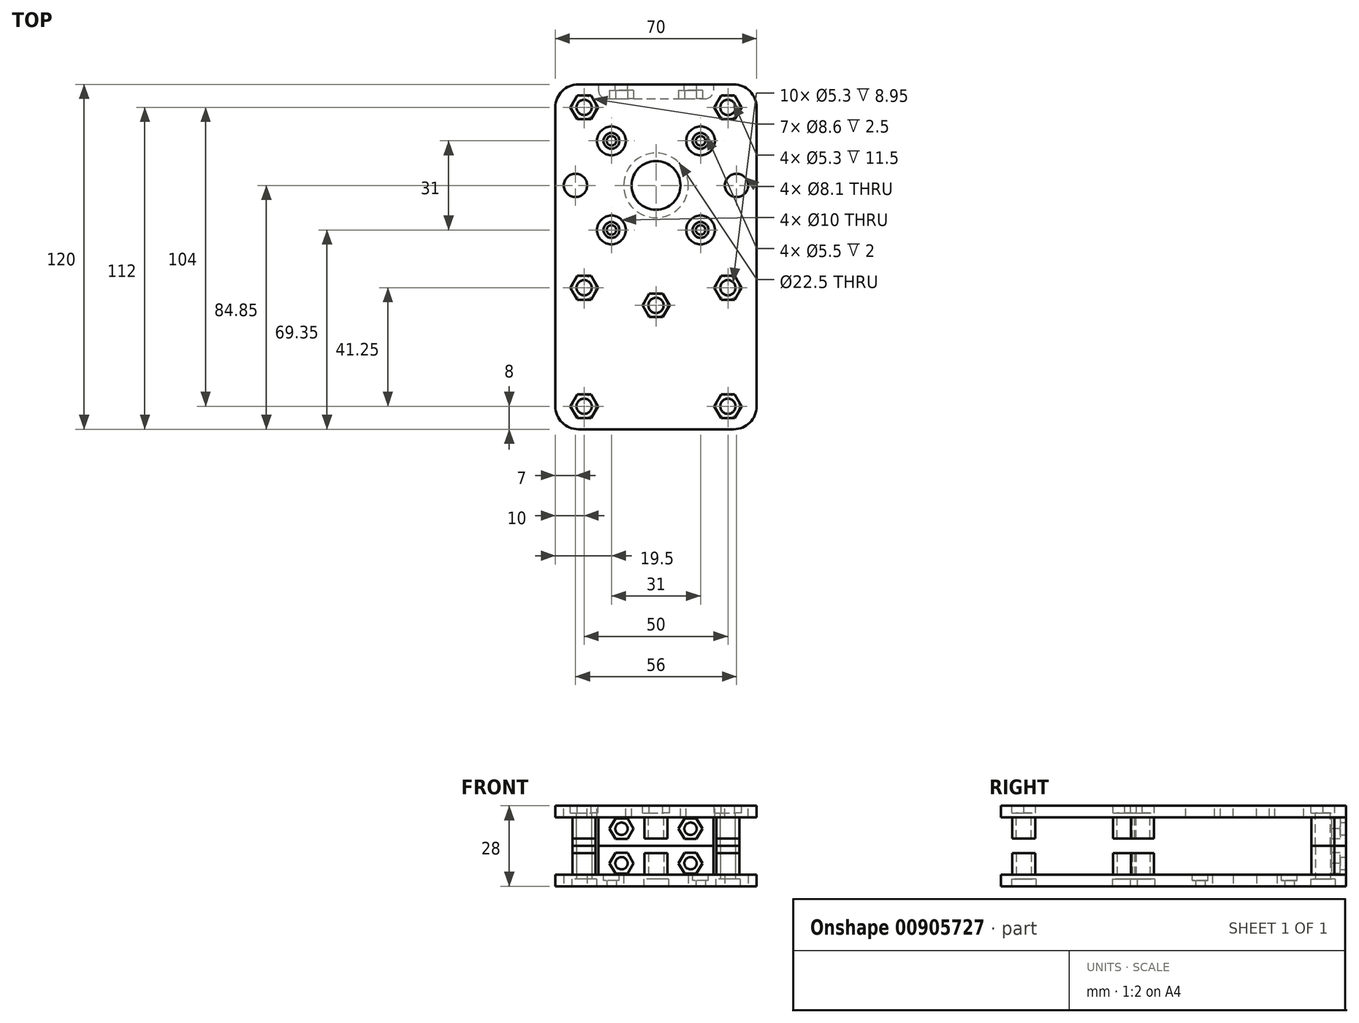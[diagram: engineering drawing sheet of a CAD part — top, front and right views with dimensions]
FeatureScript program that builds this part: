
annotation { "Feature Type Name" : "Feature", "Feature Type Description" : "" }
export const myFeature = defineFeature(function(context is Context, id is Id, definition is map)
    precondition{}
    {
        {
            var Q0;
            Q0=qCreatedBy(makeId("Top.planeOp"),FACE);
            var sketch = newSketch(context, id + "F0", { "sketchPlane" : qUnion([Q0])});
            skLineSegment(sketch, "E0.bottom", {"start": v(-35, 60) * mm, "end": v(35, 60) * mm});
            skLineSegment(sketch, "E0.top", {"start": v(-35, -60) * mm, "end": v(35, -60) * mm});
            skLineSegment(sketch, "E0.left", {"start": v(-35, 60) * mm, "end": v(-35, -60) * mm});
            skLineSegment(sketch, "E0.right", {"start": v(35, 60) * mm, "end": v(35, -60) * mm});
            skPoint(sketch, "E0.middle", {"position": v(0, 0) * mm});
            skCircle(sketch, "E1", {"center": v(-25, -52) * mm, "radius": 2.65 * mm});
            skCircle(sketch, "E2", {"center": v(25, -52) * mm, "radius": 2.65 * mm});
            skCircle(sketch, "E3", {"center": v(-25, 52) * mm, "radius": 2.65 * mm});
            skCircle(sketch, "E4", {"center": v(25, 52) * mm, "radius": 2.65 * mm});
            skCircle(sketch, "E5", {"center": v(-25, -52) * mm, "radius": 10.75 * mm, "construction": true});
            skCircle(sketch, "E6", {"center": v(25, -52) * mm, "radius": 10.75 * mm, "construction": true});
            skLineSegment(sketch, "E7.bottom", {"start": v(-50, -26.75) * mm, "end": v(50, -26.75) * mm, "construction": true});
            skLineSegment(sketch, "E7.top", {"start": v(-50, -41.75) * mm, "end": v(50, -41.75) * mm, "construction": true});
            skLineSegment(sketch, "E7.left", {"start": v(-50, -26.75) * mm, "end": v(-50, -41.75) * mm, "construction": true});
            skLineSegment(sketch, "E7.right", {"start": v(50, -26.75) * mm, "end": v(50, -41.75) * mm, "construction": true});
            skPoint(sketch, "E7.middle", {"position": v(0, -34.25) * mm});
            skLineSegment(sketch, "E8.bottom", {"start": v(-1.65, -11.6) * mm, "end": v(1.65, -11.6) * mm, "construction": true});
            skLineSegment(sketch, "E8.top", {"start": v(-1.65, -22.2) * mm, "end": v(1.65, -22.2) * mm, "construction": true});
            skLineSegment(sketch, "E8.left", {"start": v(-2.65, -12.6) * mm, "end": v(-2.65, -21.2) * mm, "construction": true});
            skLineSegment(sketch, "E8.right", {"start": v(2.65, -12.6) * mm, "end": v(2.65, -21.2) * mm, "construction": true});
            skPoint(sketch, "E8.middle", {"position": v(0, -16.9) * mm});
            skPoint(sketch, "E9.visualSharp", {"position": v(-2.65, -22.2) * mm});
            skArc(sketch, "E9.filletArc", {"start": v(-2.65, -21.2) * mm, "mid": v(-2.36, -21.9) * mm, "end": v(-1.65, -22.2) * mm, "construction": true});
            skPoint(sketch, "E10.visualSharp", {"position": v(2.65, -22.2) * mm});
            skArc(sketch, "E10.filletArc", {"start": v(1.65, -22.2) * mm, "mid": v(2.36, -21.9) * mm, "end": v(2.65, -21.2) * mm, "construction": true});
            skPoint(sketch, "E11.visualSharp", {"position": v(2.65, -11.6) * mm});
            skArc(sketch, "E11.filletArc", {"start": v(2.65, -12.6) * mm, "mid": v(2.36, -11.9) * mm, "end": v(1.65, -11.6) * mm, "construction": true});
            skPoint(sketch, "E12.visualSharp", {"position": v(-2.65, -11.6) * mm});
            skArc(sketch, "E12.filletArc", {"start": v(-1.65, -11.6) * mm, "mid": v(-2.36, -11.9) * mm, "end": v(-2.65, -12.6) * mm, "construction": true});
            skCircle(sketch, "E13", {"center": v(0, -16.9) * mm, "radius": 10.75 * mm, "construction": true});
            skCircle(sketch, "E14", {"center": v(-25, -10.75) * mm, "radius": 2.65 * mm});
            skCircle(sketch, "E15", {"center": v(25, -10.75) * mm, "radius": 2.65 * mm});
            skCircle(sketch, "E16", {"center": v(-25, -10.75) * mm, "radius": 11 * mm, "construction": true});
            skCircle(sketch, "E17", {"center": v(25, -10.75) * mm, "radius": 11 * mm, "construction": true});
            skLineSegment(sketch, "E18.bottom", {"start": v(-21.15, 46) * mm, "end": v(21.15, 46) * mm, "construction": true});
            skLineSegment(sketch, "E18.top", {"start": v(-21.15, 3.7) * mm, "end": v(21.15, 3.7) * mm, "construction": true});
            skLineSegment(sketch, "E18.left", {"start": v(-21.15, 46) * mm, "end": v(-21.15, 3.7) * mm, "construction": true});
            skLineSegment(sketch, "E18.right", {"start": v(21.15, 46) * mm, "end": v(21.15, 3.7) * mm, "construction": true});
            skPoint(sketch, "E18.middle", {"position": v(0, 24.85) * mm});
            skCircle(sketch, "E19", {"center": v(-25, 52) * mm, "radius": 4.3 * mm});
            skCircle(sketch, "E20", {"center": v(25, 52) * mm, "radius": 4.3 * mm});
            skCircle(sketch, "E21", {"center": v(-25, -10.75) * mm, "radius": 4.3 * mm});
            skCircle(sketch, "E22", {"center": v(25, -10.75) * mm, "radius": 4.3 * mm});
            skCircle(sketch, "E23", {"center": v(-25, -52) * mm, "radius": 4.3 * mm});
            skCircle(sketch, "E24", {"center": v(25, -52) * mm, "radius": 4.3 * mm});
            skCircle(sketch, "E25", {"center": v(-28, 24.85) * mm, "radius": 4.05 * mm});
            skCircle(sketch, "E26", {"center": v(28, 24.85) * mm, "radius": 4.05 * mm});
            skCircle(sketch, "E27", {"center": v(-15.5, 40.35) * mm, "radius": 1.65 * mm});
            skCircle(sketch, "E28", {"center": v(15.5, 40.35) * mm, "radius": 1.65 * mm});
            skCircle(sketch, "E29", {"center": v(15.5, 9.35) * mm, "radius": 1.65 * mm});
            skCircle(sketch, "E30", {"center": v(-15.5, 9.35) * mm, "radius": 1.65 * mm});
            skCircle(sketch, "E31", {"center": v(0, 24.85) * mm, "radius": 11.25 * mm});
            skCircle(sketch, "E32", {"center": v(0, -16.9) * mm, "radius": 2.65 * mm});
            skCircle(sketch, "E33", {"center": v(0, -16.9) * mm, "radius": 4.3 * mm});
            skSolve(sketch);
        }
        {
            var Q0;
            Q0=makeQuery(id+"F0.imprint","IMPRINT",FACE,{"disambiguationData":[TD([[makeQuery(id+"F0.imprint","IMPRINT",EDGE,{"derivedFrom":sQuery(id+"F0.wireOp",EDGE,"E0.bottom")}),-1.0]])]});
            var Q1;
            Q1=makeQuery(id+"F0.imprint","IMPRINT",FACE,{"disambiguationData":[TD([[makeQuery(id+"F0.imprint","IMPRINT",EDGE,{"derivedFrom":sQuery(id+"F0.wireOp",EDGE,"E4")}),-1.0]])]});
            var Q2;
            Q2=makeQuery(id+"F0.imprint","IMPRINT",FACE,{"disambiguationData":[TD([[makeQuery(id+"F0.imprint","IMPRINT",EDGE,{"derivedFrom":sQuery(id+"F0.wireOp",EDGE,"E3")}),-1.0]])]});
            var Q3;
            Q3=makeQuery(id+"F0.imprint","IMPRINT",FACE,{"disambiguationData":[TD([[makeQuery(id+"F0.imprint","IMPRINT",EDGE,{"derivedFrom":sQuery(id+"F0.wireOp",EDGE,"E15")}),-1.0]])]});
            var Q4;
            Q4=makeQuery(id+"F0.imprint","IMPRINT",FACE,{"disambiguationData":[TD([[makeQuery(id+"F0.imprint","IMPRINT",EDGE,{"derivedFrom":sQuery(id+"F0.wireOp",EDGE,"E14")}),-1.0]])]});
            var Q5;
            Q5=makeQuery(id+"F0.imprint","IMPRINT",FACE,{"disambiguationData":[TD([[makeQuery(id+"F0.imprint","IMPRINT",EDGE,{"derivedFrom":sQuery(id+"F0.wireOp",EDGE,"E2")}),-1.0]])]});
            var Q6;
            Q6=makeQuery(id+"F0.imprint","IMPRINT",FACE,{"disambiguationData":[TD([[makeQuery(id+"F0.imprint","IMPRINT",EDGE,{"derivedFrom":sQuery(id+"F0.wireOp",EDGE,"E1")}),-1.0]])]});
            var Q7;
            Q7=makeQuery(id+"F0.imprint","IMPRINT",FACE,{"disambiguationData":[TD([[makeQuery(id+"F0.imprint","IMPRINT",EDGE,{"derivedFrom":sQuery(id+"F0.wireOp",EDGE,"E32")}),-1.0]])]});
            extrude(context, id + "F1", {"entities" : qUnion([Q0, Q1, Q2, Q3, Q4, Q5, Q6, Q7]), "depth" : 4 * mm, "offsetDistance" : 25 * mm});
        }
        {
            var Q0;
            Q0=makeQuery(id+"F1.opExtrude","CAP_FACE",FACE,{"disambiguationData":[OSD([sQuery(id+"F0.wireOp",EDGE,"E0.bottom"),sQuery(id+"F0.wireOp",EDGE,"E0.top"),sQuery(id+"F0.wireOp",EDGE,"E0.left"),sQuery(id+"F0.wireOp",EDGE,"E0.right"),sQuery(id+"F0.wireOp",EDGE,"E1"),sQuery(id+"F0.wireOp",EDGE,"E2"),sQuery(id+"F0.wireOp",EDGE,"E3"),sQuery(id+"F0.wireOp",EDGE,"E4"),sQuery(id+"F0.wireOp",EDGE,"E8.bottom"),sQuery(id+"F0.wireOp",EDGE,"E8.top"),sQuery(id+"F0.wireOp",EDGE,"E8.left"),sQuery(id+"F0.wireOp",EDGE,"E8.right"),sQuery(id+"F0.wireOp",EDGE,"E9.filletArc"),sQuery(id+"F0.wireOp",EDGE,"E10.filletArc"),sQuery(id+"F0.wireOp",EDGE,"E11.filletArc"),sQuery(id+"F0.wireOp",EDGE,"E12.filletArc"),sQuery(id+"F0.wireOp",EDGE,"E14"),sQuery(id+"F0.wireOp",EDGE,"E15"),sQuery(id+"F0.wireOp",EDGE,"E25"),sQuery(id+"F0.wireOp",EDGE,"E26"),sQuery(id+"F0.wireOp",EDGE,"E27"),sQuery(id+"F0.wireOp",EDGE,"E28"),sQuery(id+"F0.wireOp",EDGE,"E29"),sQuery(id+"F0.wireOp",EDGE,"E30"),sQuery(id+"F0.wireOp",EDGE,"E31")])],"isStart":false});
            var sketch = newSketch(context, id + "F2", { "sketchPlane" : qUnion([Q0])});
            skCircle(sketch, "E34", {"center": v(-15.5, 40.35) * mm, "radius": 2.75 * mm});
            skCircle(sketch, "E35", {"center": v(15.5, 40.35) * mm, "radius": 2.75 * mm});
            skCircle(sketch, "E36", {"center": v(-15.5, 9.35) * mm, "radius": 2.75 * mm});
            skCircle(sketch, "E37", {"center": v(15.5, 9.35) * mm, "radius": 2.75 * mm});
            skSolve(sketch);
        }
        {
            var Q0;
            Q0=makeQuery(id+"F2.imprint","IMPRINT",FACE,{"disambiguationData":[TD([[makeQuery(id+"F2.imprint","IMPRINT",EDGE,{"derivedFrom":sQuery(id+"F2.wireOp",EDGE,"E34")}),1.0]])]});
            var Q1;
            Q1=makeQuery(id+"F2.imprint","IMPRINT",FACE,{"disambiguationData":[TD([[makeQuery(id+"F2.imprint","IMPRINT",EDGE,{"derivedFrom":sQuery(id+"F2.wireOp",EDGE,"E36")}),1.0]])]});
            var Q2;
            Q2=makeQuery(id+"F2.imprint","IMPRINT",FACE,{"disambiguationData":[TD([[makeQuery(id+"F2.imprint","IMPRINT",EDGE,{"derivedFrom":sQuery(id+"F2.wireOp",EDGE,"E37")}),1.0]])]});
            var Q3;
            Q3=makeQuery(id+"F2.imprint","IMPRINT",FACE,{"disambiguationData":[TD([[makeQuery(id+"F2.imprint","IMPRINT",EDGE,{"derivedFrom":sQuery(id+"F2.wireOp",EDGE,"E35")}),1.0]])]});
            extrude(context, id + "F3", {"entities" : qUnion([Q0, Q1, Q2, Q3]), "operationType" : NewBodyOperationType.REMOVE, "oppositeDirection" : true, "depth" : 2 * mm, "offsetDistance" : 25 * mm});
        }
        {
            var Q0;
            Q0=makeQuery(id+"F0.imprint","IMPRINT",FACE,{"disambiguationData":[TD([[makeQuery(id+"F0.imprint","IMPRINT",EDGE,{"derivedFrom":sQuery(id+"F0.wireOp",EDGE,"E4")}),-1.0]])]});
            var Q1;
            Q1=makeQuery(id+"F0.imprint","IMPRINT",FACE,{"disambiguationData":[TD([[makeQuery(id+"F0.imprint","IMPRINT",EDGE,{"derivedFrom":sQuery(id+"F0.wireOp",EDGE,"E3")}),-1.0]])]});
            var Q2;
            Q2=makeQuery(id+"F0.imprint","IMPRINT",FACE,{"disambiguationData":[TD([[makeQuery(id+"F0.imprint","IMPRINT",EDGE,{"derivedFrom":sQuery(id+"F0.wireOp",EDGE,"E15")}),-1.0]])]});
            var Q3;
            Q3=makeQuery(id+"F0.imprint","IMPRINT",FACE,{"disambiguationData":[TD([[makeQuery(id+"F0.imprint","IMPRINT",EDGE,{"derivedFrom":sQuery(id+"F0.wireOp",EDGE,"E14")}),-1.0]])]});
            var Q4;
            Q4=makeQuery(id+"F0.imprint","IMPRINT",FACE,{"disambiguationData":[TD([[makeQuery(id+"F0.imprint","IMPRINT",EDGE,{"derivedFrom":sQuery(id+"F0.wireOp",EDGE,"E2")}),-1.0]])]});
            var Q5;
            Q5=makeQuery(id+"F0.imprint","IMPRINT",FACE,{"disambiguationData":[TD([[makeQuery(id+"F0.imprint","IMPRINT",EDGE,{"derivedFrom":sQuery(id+"F0.wireOp",EDGE,"E1")}),-1.0]])]});
            extrude(context, id + "F4", {"entities" : qUnion([Q0, Q1, Q2, Q3, Q4, Q5]), "operationType" : NewBodyOperationType.REMOVE, "depth" : 2.5 * mm, "offsetDistance" : 25 * mm});
        }
        {
            var Q0;
            Q0=makeQuery(id+"FN2gQwAAYemFBsZ_1.imprint","IMPRINT",FACE,{"disambiguationData":[TD([[makeQuery(id+"FN2gQwAAYemFBsZ_1.imprint","IMPRINT",EDGE,{"derivedFrom":sQuery(id+"FN2gQwAAYemFBsZ_1.wireOp",EDGE,"b6049740-b090-4d88-954d-f700c698196f.0")}),1.0]])]});
            var Q1;
            Q1=makeQuery(id+"F0.imprint","IMPRINT",FACE,{"disambiguationData":[TD([[makeQuery(id+"F0.imprint","IMPRINT",EDGE,{"derivedFrom":sQuery(id+"F0.wireOp",EDGE,"E32")}),-1.0]])]});
            extrude(context, id + "F5", {"entities" : qUnion([Q0, Q1]), "operationType" : NewBodyOperationType.REMOVE, "depth" : 2.5 * mm, "offsetDistance" : 25 * mm});
        }
        {
            var Q0;
            Q0=makeQuery(id+"F1.opExtrude","CAP_FACE",FACE,{"disambiguationData":[OSD([sQuery(id+"F0.wireOp",EDGE,"E0.bottom"),sQuery(id+"F0.wireOp",EDGE,"E0.top"),sQuery(id+"F0.wireOp",EDGE,"E0.left"),sQuery(id+"F0.wireOp",EDGE,"E0.right"),sQuery(id+"F0.wireOp",EDGE,"E1"),sQuery(id+"F0.wireOp",EDGE,"E2"),sQuery(id+"F0.wireOp",EDGE,"E3"),sQuery(id+"F0.wireOp",EDGE,"E4"),sQuery(id+"F0.wireOp",EDGE,"E8.bottom"),sQuery(id+"F0.wireOp",EDGE,"E8.top"),sQuery(id+"F0.wireOp",EDGE,"E8.left"),sQuery(id+"F0.wireOp",EDGE,"E8.right"),sQuery(id+"F0.wireOp",EDGE,"E9.filletArc"),sQuery(id+"F0.wireOp",EDGE,"E10.filletArc"),sQuery(id+"F0.wireOp",EDGE,"E11.filletArc"),sQuery(id+"F0.wireOp",EDGE,"E12.filletArc"),sQuery(id+"F0.wireOp",EDGE,"E14"),sQuery(id+"F0.wireOp",EDGE,"E15"),sQuery(id+"F0.wireOp",EDGE,"E25"),sQuery(id+"F0.wireOp",EDGE,"E26"),sQuery(id+"F0.wireOp",EDGE,"E27"),sQuery(id+"F0.wireOp",EDGE,"E28"),sQuery(id+"F0.wireOp",EDGE,"E29"),sQuery(id+"F0.wireOp",EDGE,"E30"),sQuery(id+"F0.wireOp",EDGE,"E31")])],"isStart":false});
            var sketch = newSketch(context, id + "F6", { "sketchPlane" : qUnion([Q0])});
            skCircle(sketch, "E38", {"center": v(-25, -10.75) * mm, "radius": 4 * mm});
            skCircle(sketch, "E39", {"center": v(-25, -52) * mm, "radius": 4 * mm});
            skCircle(sketch, "E40", {"center": v(25, -52) * mm, "radius": 4 * mm});
            skCircle(sketch, "E41", {"center": v(25, -10.75) * mm, "radius": 4 * mm});
            skCircle(sketch, "E42", {"center": v(-25, 52) * mm, "radius": 4 * mm});
            skCircle(sketch, "E43", {"center": v(25, 52) * mm, "radius": 4 * mm});
            skCircle(sketch, "E44", {"center": v(0, -16.9) * mm, "radius": 4 * mm});
            skSolve(sketch);
        }
        {
            var Q0;
            Q0=makeQuery(id+"F6.imprint","IMPRINT",FACE,{"disambiguationData":[TD([[makeQuery(id+"F6.imprint","IMPRINT",EDGE,{"derivedFrom":sQuery(id+"F6.wireOp",EDGE,"E38")}),1.0]])]});
            var Q1;
            Q1=makeQuery(id+"F6.imprint","IMPRINT",FACE,{"disambiguationData":[TD([[makeQuery(id+"F6.imprint","IMPRINT",EDGE,{"derivedFrom":sQuery(id+"F6.wireOp",EDGE,"E39")}),1.0]])]});
            var Q2;
            Q2=makeQuery(id+"F6.imprint","IMPRINT",FACE,{"disambiguationData":[TD([[makeQuery(id+"F6.imprint","IMPRINT",EDGE,{"derivedFrom":sQuery(id+"F6.wireOp",EDGE,"E40")}),1.0]])]});
            var Q3;
            Q3=makeQuery(id+"F6.imprint","IMPRINT",FACE,{"disambiguationData":[TD([[makeQuery(id+"F6.imprint","IMPRINT",EDGE,{"derivedFrom":sQuery(id+"F6.wireOp",EDGE,"E41")}),1.0]])]});
            var Q4;
            Q4=makeQuery(id+"F6.imprint","IMPRINT",FACE,{"disambiguationData":[TD([[makeQuery(id+"F6.imprint","IMPRINT",EDGE,{"derivedFrom":sQuery(id+"F6.wireOp",EDGE,"E44")}),1.0]])]});
            extrude(context, id + "F7", {"entities" : qUnion([Q0, Q1, Q2, Q3, Q4]), "operationType" : NewBodyOperationType.ADD, "depth" : 7.45 * mm, "offsetDistance" : 25 * mm});
        }
        {
            var Q0;
            Q0=makeQuery(id+"F6.imprint","IMPRINT",FACE,{"disambiguationData":[TD([[makeQuery(id+"F6.imprint","IMPRINT",EDGE,{"derivedFrom":sQuery(id+"F6.wireOp",EDGE,"E42")}),1.0]])]});
            var Q1;
            Q1=makeQuery(id+"F6.imprint","IMPRINT",FACE,{"disambiguationData":[TD([[makeQuery(id+"F6.imprint","IMPRINT",EDGE,{"derivedFrom":sQuery(id+"F6.wireOp",EDGE,"E43")}),1.0]])]});
            extrude(context, id + "F8", {"entities" : qUnion([Q0, Q1]), "operationType" : NewBodyOperationType.ADD, "depth" : 10 * mm, "offsetDistance" : 25 * mm});
        }
        {
            var Q0;
            Q0=makeQuery(id+"F1.opExtrude","CAP_FACE",FACE,{"disambiguationData":[OSD([sQuery(id+"F0.wireOp",EDGE,"E0.bottom"),sQuery(id+"F0.wireOp",EDGE,"E0.top"),sQuery(id+"F0.wireOp",EDGE,"E0.left"),sQuery(id+"F0.wireOp",EDGE,"E0.right"),sQuery(id+"F0.wireOp",EDGE,"E1"),sQuery(id+"F0.wireOp",EDGE,"E2"),sQuery(id+"F0.wireOp",EDGE,"E3"),sQuery(id+"F0.wireOp",EDGE,"E4"),sQuery(id+"F0.wireOp",EDGE,"E8.bottom"),sQuery(id+"F0.wireOp",EDGE,"E8.top"),sQuery(id+"F0.wireOp",EDGE,"E8.left"),sQuery(id+"F0.wireOp",EDGE,"E8.right"),sQuery(id+"F0.wireOp",EDGE,"E9.filletArc"),sQuery(id+"F0.wireOp",EDGE,"E10.filletArc"),sQuery(id+"F0.wireOp",EDGE,"E11.filletArc"),sQuery(id+"F0.wireOp",EDGE,"E12.filletArc"),sQuery(id+"F0.wireOp",EDGE,"E14"),sQuery(id+"F0.wireOp",EDGE,"E15"),sQuery(id+"F0.wireOp",EDGE,"E25"),sQuery(id+"F0.wireOp",EDGE,"E26"),sQuery(id+"F0.wireOp",EDGE,"E27"),sQuery(id+"F0.wireOp",EDGE,"E28"),sQuery(id+"F0.wireOp",EDGE,"E29"),sQuery(id+"F0.wireOp",EDGE,"E30"),sQuery(id+"F0.wireOp",EDGE,"E31")])],"isStart":false});
            var sketch = newSketch(context, id + "F9", { "sketchPlane" : qUnion([Q0])});
            skLineSegment(sketch, "E45.bottom", {"start": v(-20, 60) * mm, "end": v(20, 60) * mm});
            skLineSegment(sketch, "E45.top", {"start": v(-17, 55) * mm, "end": v(17, 55) * mm});
            skLineSegment(sketch, "E45.left", {"start": v(-20, 60) * mm, "end": v(-20, 58) * mm});
            skLineSegment(sketch, "E45.right", {"start": v(20, 60) * mm, "end": v(20, 58) * mm});
            skPoint(sketch, "E46.visualSharp", {"position": v(-20, 55) * mm});
            skArc(sketch, "E46.filletArc", {"start": v(-20, 58) * mm, "mid": v(-19.12, 55.88) * mm, "end": v(-17, 55) * mm});
            skPoint(sketch, "E47.visualSharp", {"position": v(20, 55) * mm});
            skArc(sketch, "E47.filletArc", {"start": v(17, 55) * mm, "mid": v(19.12, 55.88) * mm, "end": v(20, 58) * mm});
            skSolve(sketch);
        }
        {
            var Q0;
            Q0=makeQuery(id+"F9.imprint","IMPRINT",FACE,{"disambiguationData":[TD([[makeQuery(id+"F9.imprint","IMPRINT",EDGE,{"derivedFrom":sQuery(id+"F9.wireOp",EDGE,"E45.bottom")}),-1.0]])]});
            extrude(context, id + "F10", {"entities" : qUnion([Q0]), "operationType" : NewBodyOperationType.ADD, "depth" : 10 * mm, "offsetDistance" : 25 * mm});
        }
        {
            var Q0;
            Q0=makeQuery(id+"F10.boolean.opBoolean","MERGE",FACE,{"derivedFrom":[makeQuery(id+"F1.opExtrude","SWEPT_FACE",FACE,{"disambiguationData":[OSD([sQuery(id+"F0.wireOp",EDGE,"E0.bottom")])]}),makeQuery(id+"F10.opExtrude","SWEPT_FACE",FACE,{"disambiguationData":[OSD([sQuery(id+"F9.wireOp",EDGE,"E45.bottom")])]})]});
            var sketch = newSketch(context, id + "F11", { "sketchPlane" : qUnion([Q0])});
            skCircle(sketch, "E48", {"center": v(12, 8) * mm, "radius": 2.15 * mm});
            skCircle(sketch, "E49", {"center": v(-12, 8) * mm, "radius": 2.15 * mm});
            skSolve(sketch);
        }
        {
            var Q0;
            Q0=makeQuery(id+"F11.imprint","IMPRINT",FACE,{"disambiguationData":[TD([[makeQuery(id+"F11.imprint","IMPRINT",EDGE,{"derivedFrom":sQuery(id+"F11.wireOp",EDGE,"E48")}),1.0]])]});
            var Q1;
            Q1=makeQuery(id+"F11.imprint","IMPRINT",FACE,{"disambiguationData":[TD([[makeQuery(id+"F11.imprint","IMPRINT",EDGE,{"derivedFrom":sQuery(id+"F11.wireOp",EDGE,"E49")}),1.0]])]});
            var Q2;
            Q2=makeQuery(id+"F10.opExtrude","SWEPT_FACE",FACE,{"disambiguationData":[OSD([sQuery(id+"F9.wireOp",EDGE,"E45.top")])]});
            extrude(context, id + "F12", {"entities" : qUnion([Q0, Q1]), "operationType" : NewBodyOperationType.REMOVE, "endBound" : BoundingType.UP_TO_SURFACE, "oppositeDirection" : true, "depth" : 25 * mm, "endBoundEntityFace" : qUnion([Q2]), "offsetDistance" : 25 * mm});
        }
        {
            var Q0;
            Q0=makeQuery(id+"F10.opExtrude","SWEPT_FACE",FACE,{"disambiguationData":[OSD([sQuery(id+"F9.wireOp",EDGE,"E45.top")])]});
            var sketch = newSketch(context, id + "F13", { "sketchPlane" : qUnion([Q0])});
            skCircle(sketch, "E50.cCircle", {"center": v(-12, 8) * mm, "radius": 3.6 * mm, "construction": true});
            skLineSegment(sketch, "E50.0", {"start": v(-14.08, 11.6) * mm, "end": v(-9.92, 11.6) * mm});
            skLineSegment(sketch, "E50.1", {"start": v(-9.92, 11.6) * mm, "end": v(-7.84, 8) * mm});
            skLineSegment(sketch, "E50.2", {"start": v(-7.84, 8) * mm, "end": v(-9.92, 4.4) * mm});
            skLineSegment(sketch, "E50.3", {"start": v(-9.92, 4.4) * mm, "end": v(-14.08, 4.4) * mm});
            skLineSegment(sketch, "E50.4", {"start": v(-14.08, 4.4) * mm, "end": v(-16.16, 8) * mm});
            skLineSegment(sketch, "E50.5", {"start": v(-16.16, 8) * mm, "end": v(-14.08, 11.6) * mm});
            skPoint(sketch, "E50.0.midPoint", {"position": v(-12, 11.6) * mm});
            skCircle(sketch, "E51.cCircle", {"center": v(12, 8) * mm, "radius": 3.6 * mm, "construction": true});
            skLineSegment(sketch, "E51.0", {"start": v(9.92, 11.6) * mm, "end": v(14.08, 11.6) * mm});
            skLineSegment(sketch, "E51.1", {"start": v(14.08, 11.6) * mm, "end": v(16.16, 8) * mm});
            skLineSegment(sketch, "E51.2", {"start": v(16.16, 8) * mm, "end": v(14.08, 4.4) * mm});
            skLineSegment(sketch, "E51.3", {"start": v(14.08, 4.4) * mm, "end": v(9.92, 4.4) * mm});
            skLineSegment(sketch, "E51.4", {"start": v(9.92, 4.4) * mm, "end": v(7.84, 8) * mm});
            skLineSegment(sketch, "E51.5", {"start": v(7.84, 8) * mm, "end": v(9.92, 11.6) * mm});
            skPoint(sketch, "E51.0.midPoint", {"position": v(12, 11.6) * mm});
            skSolve(sketch);
        }
        {
            var Q0;
            Q0=makeQuery(id+"F13.imprint","IMPRINT",FACE,{"disambiguationData":[TD([[makeQuery(id+"F13.imprint","IMPRINT",EDGE,{"derivedFrom":sQuery(id+"F13.wireOp",EDGE,"E51.0")}),-1.0]])]});
            var Q1;
            Q1=makeQuery(id+"F13.imprint","IMPRINT",FACE,{"disambiguationData":[TD([[makeQuery(id+"F13.imprint","IMPRINT",EDGE,{"derivedFrom":sQuery(id+"F13.wireOp",EDGE,"E50.0")}),-1.0]])]});
            extrude(context, id + "F14", {"entities" : qUnion([Q0, Q1]), "operationType" : NewBodyOperationType.REMOVE, "oppositeDirection" : true, "depth" : 3 * mm, "offsetDistance" : 25 * mm});
        }
        {
            var Q0;
            Q0=makeQuery(id+"F1.opExtrude","SWEPT_BODY",BODY,{"disambiguationData":[OSD([sQuery(id+"F0.wireOp",EDGE,"E0.bottom"),sQuery(id+"F0.wireOp",EDGE,"E0.top"),sQuery(id+"F0.wireOp",EDGE,"E0.left"),sQuery(id+"F0.wireOp",EDGE,"E0.right"),sQuery(id+"F0.wireOp",EDGE,"E1"),sQuery(id+"F0.wireOp",EDGE,"E2"),sQuery(id+"F0.wireOp",EDGE,"E3"),sQuery(id+"F0.wireOp",EDGE,"E4"),sQuery(id+"F0.wireOp",EDGE,"E8.bottom"),sQuery(id+"F0.wireOp",EDGE,"E8.top"),sQuery(id+"F0.wireOp",EDGE,"E8.left"),sQuery(id+"F0.wireOp",EDGE,"E8.right"),sQuery(id+"F0.wireOp",EDGE,"E9.filletArc"),sQuery(id+"F0.wireOp",EDGE,"E10.filletArc"),sQuery(id+"F0.wireOp",EDGE,"E11.filletArc"),sQuery(id+"F0.wireOp",EDGE,"E12.filletArc"),sQuery(id+"F0.wireOp",EDGE,"E14"),sQuery(id+"F0.wireOp",EDGE,"E15"),sQuery(id+"F0.wireOp",EDGE,"E25"),sQuery(id+"F0.wireOp",EDGE,"E26"),sQuery(id+"F0.wireOp",EDGE,"E27"),sQuery(id+"F0.wireOp",EDGE,"E28"),sQuery(id+"F0.wireOp",EDGE,"E29"),sQuery(id+"F0.wireOp",EDGE,"E30"),sQuery(id+"F0.wireOp",EDGE,"E31")])]});
            var Q1;
            Q1=makeQuery(id+"F8.opExtrude","CAP_FACE",FACE,{"disambiguationData":[OSD([sQuery(id+"F0.wireOp",EDGE,"E3"),sQuery(id+"F6.wireOp",EDGE,"E42")])],"isStart":false});
            mirror(context, id + "F15", {"entities" : qUnion([Q0]), "mirrorPlane" : qUnion([Q1])});
        }
        {
            var Q0;
            Q0=makeQuery(id+"F15.opPattern","COPY",FACE,{"derivedFrom":makeQuery(id+"F4.boolean.opBoolean","COPY",FACE,{"derivedFrom":makeQuery(id+"F4.opExtrude","CAP_FACE",FACE,{"disambiguationData":[OSD([sQuery(id+"F0.wireOp",EDGE,"E14"),sQuery(id+"F0.wireOp",EDGE,"E21")])],"isStart":false})}),"instanceName":"1"});
            var Q1;
            Q1=makeQuery(id+"F15.opPattern","COPY",FACE,{"derivedFrom":makeQuery(id+"F4.boolean.opBoolean","COPY",FACE,{"derivedFrom":makeQuery(id+"F4.opExtrude","CAP_FACE",FACE,{"disambiguationData":[OSD([sQuery(id+"F0.wireOp",EDGE,"E1"),sQuery(id+"F0.wireOp",EDGE,"E23")])],"isStart":false})}),"instanceName":"1"});
            var Q2;
            Q2=makeQuery(id+"F15.opPattern","COPY",FACE,{"derivedFrom":makeQuery(id+"F4.boolean.opBoolean","COPY",FACE,{"derivedFrom":makeQuery(id+"F4.opExtrude","CAP_FACE",FACE,{"disambiguationData":[OSD([sQuery(id+"F0.wireOp",EDGE,"E2"),sQuery(id+"F0.wireOp",EDGE,"E24")])],"isStart":false})}),"instanceName":"1"});
            var Q3;
            Q3=makeQuery(id+"F15.opPattern","COPY",FACE,{"derivedFrom":makeQuery(id+"F4.boolean.opBoolean","COPY",FACE,{"derivedFrom":makeQuery(id+"F4.opExtrude","CAP_FACE",FACE,{"disambiguationData":[OSD([sQuery(id+"F0.wireOp",EDGE,"E15"),sQuery(id+"F0.wireOp",EDGE,"E22")])],"isStart":false})}),"instanceName":"1"});
            var Q4;
            Q4=makeQuery(id+"F15.opPattern","COPY",FACE,{"derivedFrom":makeQuery(id+"F4.boolean.opBoolean","COPY",FACE,{"derivedFrom":makeQuery(id+"F4.opExtrude","CAP_FACE",FACE,{"disambiguationData":[OSD([sQuery(id+"F0.wireOp",EDGE,"E3"),sQuery(id+"F0.wireOp",EDGE,"E19")])],"isStart":false})}),"instanceName":"1"});
            var Q5;
            Q5=makeQuery(id+"F15.opPattern","COPY",FACE,{"derivedFrom":makeQuery(id+"F4.boolean.opBoolean","COPY",FACE,{"derivedFrom":makeQuery(id+"F4.opExtrude","CAP_FACE",FACE,{"disambiguationData":[OSD([sQuery(id+"F0.wireOp",EDGE,"E4"),sQuery(id+"F0.wireOp",EDGE,"E20")])],"isStart":false})}),"instanceName":"1"});
            var Q6;
            Q6=makeQuery(id+"F15.opPattern","COPY",FACE,{"derivedFrom":makeQuery(id+"F5.boolean.opBoolean","COPY",FACE,{"derivedFrom":makeQuery(id+"F5.opExtrude","CAP_FACE",FACE,{"disambiguationData":[OSD([sQuery(id+"FN2gQwAAYemFBsZ_1.wireOp",EDGE,"b6049740-b090-4d88-954d-f700c698196f.0"),sQuery(id+"FN2gQwAAYemFBsZ_1.wireOp",EDGE,"f422f45c-7bf5-412d-89e3-80266b48b357.0"),sQuery(id+"FN2gQwAAYemFBsZ_1.wireOp",EDGE,"efcb35ef-2e5b-4bb8-b79f-5e92435b3e5b.0"),sQuery(id+"FN2gQwAAYemFBsZ_1.wireOp",EDGE,"1646675d-dff0-4150-a587-2e2e2abf0155.0"),sQuery(id+"FN2gQwAAYemFBsZ_1.wireOp",EDGE,"c82016d3-8c5d-4273-b2c0-3a98afdc202d.0"),sQuery(id+"FN2gQwAAYemFBsZ_1.wireOp",EDGE,"76cfad24-abf5-450d-8950-0da708049a1b.0"),sQuery(id+"FN2gQwAAYemFBsZ_1.wireOp",EDGE,"2f079088-94a9-4a35-b1d6-c113e9922d5e.0"),sQuery(id+"FN2gQwAAYemFBsZ_1.wireOp",EDGE,"c33eaa7b-eaf1-4da6-90ec-c160ff7c63d3.0"),sQuery(id+"FN2gQwAAYemFBsZ_1.wireOp",EDGE,"f0ed33f3-9ef4-43dd-9b29-648670789cae.0"),sQuery(id+"FN2gQwAAYemFBsZ_1.wireOp",EDGE,"f0ed33f3-9ef4-43dd-9b29-648670789cae.1"),sQuery(id+"FN2gQwAAYemFBsZ_1.wireOp",EDGE,"f0ed33f3-9ef4-43dd-9b29-648670789cae.2"),sQuery(id+"FN2gQwAAYemFBsZ_1.wireOp",EDGE,"f0ed33f3-9ef4-43dd-9b29-648670789cae.3"),sQuery(id+"FN2gQwAAYemFBsZ_1.wireOp",EDGE,"f0ed33f3-9ef4-43dd-9b29-648670789cae.4"),sQuery(id+"FN2gQwAAYemFBsZ_1.wireOp",EDGE,"f0ed33f3-9ef4-43dd-9b29-648670789cae.5"),sQuery(id+"FN2gQwAAYemFBsZ_1.wireOp",EDGE,"f0ed33f3-9ef4-43dd-9b29-648670789cae.6"),sQuery(id+"FN2gQwAAYemFBsZ_1.wireOp",EDGE,"f0ed33f3-9ef4-43dd-9b29-648670789cae.7")])],"isStart":false})}),"instanceName":"1"});
            var Q7;
            Q7=makeQuery(id+"F15.opPattern","COPY",FACE,{"derivedFrom":makeQuery(id+"F1.opExtrude","CAP_FACE",FACE,{"disambiguationData":[OSD([sQuery(id+"F0.wireOp",EDGE,"E0.bottom"),sQuery(id+"F0.wireOp",EDGE,"E0.top"),sQuery(id+"F0.wireOp",EDGE,"E0.left"),sQuery(id+"F0.wireOp",EDGE,"E0.right"),sQuery(id+"F0.wireOp",EDGE,"E1"),sQuery(id+"F0.wireOp",EDGE,"E2"),sQuery(id+"F0.wireOp",EDGE,"E3"),sQuery(id+"F0.wireOp",EDGE,"E4"),sQuery(id+"F0.wireOp",EDGE,"E8.bottom"),sQuery(id+"F0.wireOp",EDGE,"E8.top"),sQuery(id+"F0.wireOp",EDGE,"E8.left"),sQuery(id+"F0.wireOp",EDGE,"E8.right"),sQuery(id+"F0.wireOp",EDGE,"E9.filletArc"),sQuery(id+"F0.wireOp",EDGE,"E10.filletArc"),sQuery(id+"F0.wireOp",EDGE,"E11.filletArc"),sQuery(id+"F0.wireOp",EDGE,"E12.filletArc"),sQuery(id+"F0.wireOp",EDGE,"E14"),sQuery(id+"F0.wireOp",EDGE,"E15"),sQuery(id+"F0.wireOp",EDGE,"E25"),sQuery(id+"F0.wireOp",EDGE,"E26"),sQuery(id+"F0.wireOp",EDGE,"E27"),sQuery(id+"F0.wireOp",EDGE,"E28"),sQuery(id+"F0.wireOp",EDGE,"E29"),sQuery(id+"F0.wireOp",EDGE,"E30"),sQuery(id+"F0.wireOp",EDGE,"E31")])],"isStart":true}),"instanceName":"1"});
            extrude(context, id + "F16", {"entities" : qUnion([Q0, Q1, Q2, Q3, Q4, Q5, Q6]), "operationType" : NewBodyOperationType.ADD, "endBound" : BoundingType.UP_TO_SURFACE, "depth" : 25 * mm, "endBoundEntityFace" : qUnion([Q7]), "offsetDistance" : 25 * mm});
        }
        {
            var Q0;
            {var subQ0=sQuery(id+"F0.wireOp",EDGE,"E15");var subQ1=sQuery(id+"F0.wireOp",EDGE,"E14");var subQ2=sQuery(id+"F0.wireOp",EDGE,"E4");var subQ3=sQuery(id+"F0.wireOp",EDGE,"E3");var subQ4=sQuery(id+"F0.wireOp",EDGE,"E2");var subQ5=sQuery(id+"F0.wireOp",EDGE,"E1");Q0=makeQuery(id+"F16.boolean.opBoolean","MERGE",FACE,{"derivedFrom":[makeQuery(id+"F15.opPattern","COPY",FACE,{"derivedFrom":makeQuery(id+"F1.opExtrude","CAP_FACE",FACE,{"disambiguationData":[OSD([sQuery(id+"F0.wireOp",EDGE,"E0.bottom"),sQuery(id+"F0.wireOp",EDGE,"E0.top"),sQuery(id+"F0.wireOp",EDGE,"E0.left"),sQuery(id+"F0.wireOp",EDGE,"E0.right"),subQ5,subQ4,subQ3,subQ2,sQuery(id+"F0.wireOp",EDGE,"E8.bottom"),sQuery(id+"F0.wireOp",EDGE,"E8.top"),sQuery(id+"F0.wireOp",EDGE,"E8.left"),sQuery(id+"F0.wireOp",EDGE,"E8.right"),sQuery(id+"F0.wireOp",EDGE,"E9.filletArc"),sQuery(id+"F0.wireOp",EDGE,"E10.filletArc"),sQuery(id+"F0.wireOp",EDGE,"E11.filletArc"),sQuery(id+"F0.wireOp",EDGE,"E12.filletArc"),subQ1,subQ0,sQuery(id+"F0.wireOp",EDGE,"E25"),sQuery(id+"F0.wireOp",EDGE,"E26"),sQuery(id+"F0.wireOp",EDGE,"E27"),sQuery(id+"F0.wireOp",EDGE,"E28"),sQuery(id+"F0.wireOp",EDGE,"E29"),sQuery(id+"F0.wireOp",EDGE,"E30"),sQuery(id+"F0.wireOp",EDGE,"E31")])],"isStart":true}),"instanceName":"1"}),makeQuery(id+"F16.opExtrude","CAP_FACE",FACE,{"disambiguationData":[OSD([subQ5,sQuery(id+"F0.wireOp",EDGE,"E23")])],"isStart":false}),makeQuery(id+"F16.opExtrude","CAP_FACE",FACE,{"disambiguationData":[OSD([subQ4,sQuery(id+"F0.wireOp",EDGE,"E24")])],"isStart":false}),makeQuery(id+"F16.opExtrude","CAP_FACE",FACE,{"disambiguationData":[OSD([subQ3,sQuery(id+"F0.wireOp",EDGE,"E19")])],"isStart":false}),makeQuery(id+"F16.opExtrude","CAP_FACE",FACE,{"disambiguationData":[OSD([subQ2,sQuery(id+"F0.wireOp",EDGE,"E20")])],"isStart":false}),makeQuery(id+"F16.opExtrude","CAP_FACE",FACE,{"disambiguationData":[OSD([subQ1,sQuery(id+"F0.wireOp",EDGE,"E21")])],"isStart":false}),makeQuery(id+"F16.opExtrude","CAP_FACE",FACE,{"disambiguationData":[OSD([subQ0,sQuery(id+"F0.wireOp",EDGE,"E22")])],"isStart":false}),makeQuery(id+"F16.opExtrude","CAP_FACE",FACE,{"disambiguationData":[OSD([sQuery(id+"FN2gQwAAYemFBsZ_1.wireOp",EDGE,"b6049740-b090-4d88-954d-f700c698196f.0"),sQuery(id+"FN2gQwAAYemFBsZ_1.wireOp",EDGE,"f422f45c-7bf5-412d-89e3-80266b48b357.0"),sQuery(id+"FN2gQwAAYemFBsZ_1.wireOp",EDGE,"efcb35ef-2e5b-4bb8-b79f-5e92435b3e5b.0"),sQuery(id+"FN2gQwAAYemFBsZ_1.wireOp",EDGE,"1646675d-dff0-4150-a587-2e2e2abf0155.0"),sQuery(id+"FN2gQwAAYemFBsZ_1.wireOp",EDGE,"c82016d3-8c5d-4273-b2c0-3a98afdc202d.0"),sQuery(id+"FN2gQwAAYemFBsZ_1.wireOp",EDGE,"76cfad24-abf5-450d-8950-0da708049a1b.0"),sQuery(id+"FN2gQwAAYemFBsZ_1.wireOp",EDGE,"2f079088-94a9-4a35-b1d6-c113e9922d5e.0"),sQuery(id+"FN2gQwAAYemFBsZ_1.wireOp",EDGE,"c33eaa7b-eaf1-4da6-90ec-c160ff7c63d3.0"),sQuery(id+"FN2gQwAAYemFBsZ_1.wireOp",EDGE,"f0ed33f3-9ef4-43dd-9b29-648670789cae.0"),sQuery(id+"FN2gQwAAYemFBsZ_1.wireOp",EDGE,"f0ed33f3-9ef4-43dd-9b29-648670789cae.1"),sQuery(id+"FN2gQwAAYemFBsZ_1.wireOp",EDGE,"f0ed33f3-9ef4-43dd-9b29-648670789cae.2"),sQuery(id+"FN2gQwAAYemFBsZ_1.wireOp",EDGE,"f0ed33f3-9ef4-43dd-9b29-648670789cae.3"),sQuery(id+"FN2gQwAAYemFBsZ_1.wireOp",EDGE,"f0ed33f3-9ef4-43dd-9b29-648670789cae.4"),sQuery(id+"FN2gQwAAYemFBsZ_1.wireOp",EDGE,"f0ed33f3-9ef4-43dd-9b29-648670789cae.5"),sQuery(id+"FN2gQwAAYemFBsZ_1.wireOp",EDGE,"f0ed33f3-9ef4-43dd-9b29-648670789cae.6"),sQuery(id+"FN2gQwAAYemFBsZ_1.wireOp",EDGE,"f0ed33f3-9ef4-43dd-9b29-648670789cae.7")])],"isStart":false})]});}
            var sketch = newSketch(context, id + "F17", { "sketchPlane" : qUnion([Q0])});
            skCircle(sketch, "E52", {"center": v(-15.5, 40.35) * mm, "radius": 5 * mm});
            skCircle(sketch, "E53", {"center": v(15.5, 40.35) * mm, "radius": 5 * mm});
            skCircle(sketch, "E54", {"center": v(-15.5, 9.35) * mm, "radius": 5 * mm});
            skCircle(sketch, "E55", {"center": v(15.5, 9.35) * mm, "radius": 5 * mm});
            skCircle(sketch, "E56", {"center": v(0, 24.85) * mm, "radius": 8.5 * mm});
            skSolve(sketch);
        }
        {
            var Q0;
            Q0=makeQuery(id+"F17.imprint","IMPRINT",FACE,{"disambiguationData":[TD([[makeQuery(id+"F17.imprint","IMPRINT",EDGE,{"derivedFrom":sQuery(id+"F17.wireOp",EDGE,"E52")}),1.0]])]});
            var Q1;
            Q1=makeQuery(id+"F17.imprint","IMPRINT",FACE,{"disambiguationData":[TD([[makeQuery(id+"F17.imprint","IMPRINT",EDGE,{"derivedFrom":sQuery(id+"F17.wireOp",EDGE,"E53")}),1.0]])]});
            var Q2;
            Q2=makeQuery(id+"F17.imprint","IMPRINT",FACE,{"disambiguationData":[TD([[makeQuery(id+"F17.imprint","IMPRINT",EDGE,{"derivedFrom":sQuery(id+"F17.wireOp",EDGE,"E55")}),1.0]])]});
            var Q3;
            Q3=makeQuery(id+"F17.imprint","IMPRINT",FACE,{"disambiguationData":[TD([[makeQuery(id+"F17.imprint","IMPRINT",EDGE,{"derivedFrom":sQuery(id+"F17.wireOp",EDGE,"E54")}),1.0]])]});
            extrude(context, id + "F18", {"entities" : qUnion([Q0, Q1, Q2, Q3]), "operationType" : NewBodyOperationType.REMOVE, "endBound" : BoundingType.UP_TO_NEXT, "oppositeDirection" : true, "depth" : 25 * mm, "offsetDistance" : 25 * mm});
        }
        {
            var Q0;
            Q0=makeQuery(id+"F17.imprint","IMPRINT",FACE,{"disambiguationData":[TD([[makeQuery(id+"F17.imprint","IMPRINT",EDGE,{"derivedFrom":sQuery(id+"F17.wireOp",EDGE,"E56")}),-1.0]])]});
            var Q1;
            Q1=makeQuery(id+"F15.opPattern","COPY",FACE,{"derivedFrom":makeQuery(id+"F1.opExtrude","CAP_FACE",FACE,{"disambiguationData":[OSD([sQuery(id+"F0.wireOp",EDGE,"E0.bottom"),sQuery(id+"F0.wireOp",EDGE,"E0.top"),sQuery(id+"F0.wireOp",EDGE,"E0.left"),sQuery(id+"F0.wireOp",EDGE,"E0.right"),sQuery(id+"F0.wireOp",EDGE,"E1"),sQuery(id+"F0.wireOp",EDGE,"E2"),sQuery(id+"F0.wireOp",EDGE,"E3"),sQuery(id+"F0.wireOp",EDGE,"E4"),sQuery(id+"F0.wireOp",EDGE,"E8.bottom"),sQuery(id+"F0.wireOp",EDGE,"E8.top"),sQuery(id+"F0.wireOp",EDGE,"E8.left"),sQuery(id+"F0.wireOp",EDGE,"E8.right"),sQuery(id+"F0.wireOp",EDGE,"E9.filletArc"),sQuery(id+"F0.wireOp",EDGE,"E10.filletArc"),sQuery(id+"F0.wireOp",EDGE,"E11.filletArc"),sQuery(id+"F0.wireOp",EDGE,"E12.filletArc"),sQuery(id+"F0.wireOp",EDGE,"E14"),sQuery(id+"F0.wireOp",EDGE,"E15"),sQuery(id+"F0.wireOp",EDGE,"E25"),sQuery(id+"F0.wireOp",EDGE,"E26"),sQuery(id+"F0.wireOp",EDGE,"E27"),sQuery(id+"F0.wireOp",EDGE,"E28"),sQuery(id+"F0.wireOp",EDGE,"E29"),sQuery(id+"F0.wireOp",EDGE,"E30"),sQuery(id+"F0.wireOp",EDGE,"E31")])],"isStart":false}),"instanceName":"1"});
            extrude(context, id + "F19", {"entities" : qUnion([Q0]), "operationType" : NewBodyOperationType.ADD, "endBound" : BoundingType.UP_TO_SURFACE, "oppositeDirection" : true, "depth" : 25 * mm, "endBoundEntityFace" : qUnion([Q1]), "offsetDistance" : 25 * mm});
        }
        {
            var Q0;
            {var subQ0=sQuery(id+"F0.wireOp",EDGE,"E31");var subQ1=sQuery(id+"F0.wireOp",EDGE,"E15");var subQ2=sQuery(id+"F0.wireOp",EDGE,"E14");var subQ3=sQuery(id+"F0.wireOp",EDGE,"E4");var subQ4=sQuery(id+"F0.wireOp",EDGE,"E3");var subQ5=sQuery(id+"F0.wireOp",EDGE,"E2");var subQ6=sQuery(id+"F0.wireOp",EDGE,"E1");Q0=makeQuery(id+"F19.boolean.opBoolean","MERGE",FACE,{"derivedFrom":[makeQuery(id+"F16.boolean.opBoolean","MERGE",FACE,{"derivedFrom":[makeQuery(id+"F15.opPattern","COPY",FACE,{"derivedFrom":makeQuery(id+"F1.opExtrude","CAP_FACE",FACE,{"disambiguationData":[OSD([sQuery(id+"F0.wireOp",EDGE,"E0.bottom"),sQuery(id+"F0.wireOp",EDGE,"E0.top"),sQuery(id+"F0.wireOp",EDGE,"E0.left"),sQuery(id+"F0.wireOp",EDGE,"E0.right"),subQ6,subQ5,subQ4,subQ3,sQuery(id+"F0.wireOp",EDGE,"E8.bottom"),sQuery(id+"F0.wireOp",EDGE,"E8.top"),sQuery(id+"F0.wireOp",EDGE,"E8.left"),sQuery(id+"F0.wireOp",EDGE,"E8.right"),sQuery(id+"F0.wireOp",EDGE,"E9.filletArc"),sQuery(id+"F0.wireOp",EDGE,"E10.filletArc"),sQuery(id+"F0.wireOp",EDGE,"E11.filletArc"),sQuery(id+"F0.wireOp",EDGE,"E12.filletArc"),subQ2,subQ1,sQuery(id+"F0.wireOp",EDGE,"E25"),sQuery(id+"F0.wireOp",EDGE,"E26"),sQuery(id+"F0.wireOp",EDGE,"E27"),sQuery(id+"F0.wireOp",EDGE,"E28"),sQuery(id+"F0.wireOp",EDGE,"E29"),sQuery(id+"F0.wireOp",EDGE,"E30"),subQ0])],"isStart":true}),"instanceName":"1"}),makeQuery(id+"F16.opExtrude","CAP_FACE",FACE,{"disambiguationData":[OSD([subQ6,sQuery(id+"F0.wireOp",EDGE,"E23")])],"isStart":false}),makeQuery(id+"F16.opExtrude","CAP_FACE",FACE,{"disambiguationData":[OSD([subQ5,sQuery(id+"F0.wireOp",EDGE,"E24")])],"isStart":false}),makeQuery(id+"F16.opExtrude","CAP_FACE",FACE,{"disambiguationData":[OSD([subQ4,sQuery(id+"F0.wireOp",EDGE,"E19")])],"isStart":false}),makeQuery(id+"F16.opExtrude","CAP_FACE",FACE,{"disambiguationData":[OSD([subQ3,sQuery(id+"F0.wireOp",EDGE,"E20")])],"isStart":false}),makeQuery(id+"F16.opExtrude","CAP_FACE",FACE,{"disambiguationData":[OSD([subQ2,sQuery(id+"F0.wireOp",EDGE,"E21")])],"isStart":false}),makeQuery(id+"F16.opExtrude","CAP_FACE",FACE,{"disambiguationData":[OSD([subQ1,sQuery(id+"F0.wireOp",EDGE,"E22")])],"isStart":false}),makeQuery(id+"F16.opExtrude","CAP_FACE",FACE,{"disambiguationData":[OSD([sQuery(id+"FN2gQwAAYemFBsZ_1.wireOp",EDGE,"b6049740-b090-4d88-954d-f700c698196f.0"),sQuery(id+"FN2gQwAAYemFBsZ_1.wireOp",EDGE,"f422f45c-7bf5-412d-89e3-80266b48b357.0"),sQuery(id+"FN2gQwAAYemFBsZ_1.wireOp",EDGE,"efcb35ef-2e5b-4bb8-b79f-5e92435b3e5b.0"),sQuery(id+"FN2gQwAAYemFBsZ_1.wireOp",EDGE,"1646675d-dff0-4150-a587-2e2e2abf0155.0"),sQuery(id+"FN2gQwAAYemFBsZ_1.wireOp",EDGE,"c82016d3-8c5d-4273-b2c0-3a98afdc202d.0"),sQuery(id+"FN2gQwAAYemFBsZ_1.wireOp",EDGE,"76cfad24-abf5-450d-8950-0da708049a1b.0"),sQuery(id+"FN2gQwAAYemFBsZ_1.wireOp",EDGE,"2f079088-94a9-4a35-b1d6-c113e9922d5e.0"),sQuery(id+"FN2gQwAAYemFBsZ_1.wireOp",EDGE,"c33eaa7b-eaf1-4da6-90ec-c160ff7c63d3.0"),sQuery(id+"FN2gQwAAYemFBsZ_1.wireOp",EDGE,"f0ed33f3-9ef4-43dd-9b29-648670789cae.0"),sQuery(id+"FN2gQwAAYemFBsZ_1.wireOp",EDGE,"f0ed33f3-9ef4-43dd-9b29-648670789cae.1"),sQuery(id+"FN2gQwAAYemFBsZ_1.wireOp",EDGE,"f0ed33f3-9ef4-43dd-9b29-648670789cae.2"),sQuery(id+"FN2gQwAAYemFBsZ_1.wireOp",EDGE,"f0ed33f3-9ef4-43dd-9b29-648670789cae.3"),sQuery(id+"FN2gQwAAYemFBsZ_1.wireOp",EDGE,"f0ed33f3-9ef4-43dd-9b29-648670789cae.4"),sQuery(id+"FN2gQwAAYemFBsZ_1.wireOp",EDGE,"f0ed33f3-9ef4-43dd-9b29-648670789cae.5"),sQuery(id+"FN2gQwAAYemFBsZ_1.wireOp",EDGE,"f0ed33f3-9ef4-43dd-9b29-648670789cae.6"),sQuery(id+"FN2gQwAAYemFBsZ_1.wireOp",EDGE,"f0ed33f3-9ef4-43dd-9b29-648670789cae.7")])],"isStart":false})]}),makeQuery(id+"F19.opExtrude","CAP_FACE",FACE,{"disambiguationData":[OSD([subQ0,sQuery(id+"F17.wireOp",EDGE,"E56")])],"isStart":true})]});}
            var sketch = newSketch(context, id + "F20", { "sketchPlane" : qUnion([Q0])});
            skCircle(sketch, "E57.cCircle", {"center": v(-25, 52) * mm, "radius": 4.15 * mm, "construction": true});
            skLineSegment(sketch, "E57.0", {"start": v(-27.4, 56.15) * mm, "end": v(-22.6, 56.15) * mm});
            skLineSegment(sketch, "E57.1", {"start": v(-22.6, 56.15) * mm, "end": v(-20.2, 52) * mm});
            skLineSegment(sketch, "E57.2", {"start": v(-20.2, 52) * mm, "end": v(-22.6, 47.85) * mm});
            skLineSegment(sketch, "E57.3", {"start": v(-22.6, 47.85) * mm, "end": v(-27.4, 47.85) * mm});
            skLineSegment(sketch, "E57.4", {"start": v(-27.4, 47.85) * mm, "end": v(-29.8, 52) * mm});
            skLineSegment(sketch, "E57.5", {"start": v(-29.8, 52) * mm, "end": v(-27.4, 56.15) * mm});
            skPoint(sketch, "E57.0.midPoint", {"position": v(-25, 56.15) * mm});
            skCircle(sketch, "E58.cCircle", {"center": v(25, 52) * mm, "radius": 4.15 * mm, "construction": true});
            skLineSegment(sketch, "E58.0", {"start": v(22.6, 56.15) * mm, "end": v(27.4, 56.15) * mm});
            skLineSegment(sketch, "E58.1", {"start": v(27.4, 56.15) * mm, "end": v(29.8, 52) * mm});
            skLineSegment(sketch, "E58.2", {"start": v(29.8, 52) * mm, "end": v(27.4, 47.85) * mm});
            skLineSegment(sketch, "E58.3", {"start": v(27.4, 47.85) * mm, "end": v(22.6, 47.85) * mm});
            skLineSegment(sketch, "E58.4", {"start": v(22.6, 47.85) * mm, "end": v(20.2, 52) * mm});
            skLineSegment(sketch, "E58.5", {"start": v(20.2, 52) * mm, "end": v(22.6, 56.15) * mm});
            skPoint(sketch, "E58.0.midPoint", {"position": v(25, 56.15) * mm});
            skCircle(sketch, "E59.cCircle", {"center": v(-25, -10.75) * mm, "radius": 4.15 * mm, "construction": true});
            skLineSegment(sketch, "E59.0", {"start": v(-27.4, -6.6) * mm, "end": v(-22.6, -6.6) * mm});
            skLineSegment(sketch, "E59.1", {"start": v(-22.6, -6.6) * mm, "end": v(-20.2, -10.75) * mm});
            skLineSegment(sketch, "E59.2", {"start": v(-20.2, -10.75) * mm, "end": v(-22.6, -14.9) * mm});
            skLineSegment(sketch, "E59.3", {"start": v(-22.6, -14.9) * mm, "end": v(-27.4, -14.9) * mm});
            skLineSegment(sketch, "E59.4", {"start": v(-27.4, -14.9) * mm, "end": v(-29.8, -10.75) * mm});
            skLineSegment(sketch, "E59.5", {"start": v(-29.8, -10.75) * mm, "end": v(-27.4, -6.6) * mm});
            skPoint(sketch, "E59.0.midPoint", {"position": v(-25, -6.6) * mm});
            skCircle(sketch, "E60.cCircle", {"center": v(-25, -52) * mm, "radius": 4.15 * mm, "construction": true});
            skLineSegment(sketch, "E60.0", {"start": v(-27.4, -47.85) * mm, "end": v(-22.6, -47.85) * mm});
            skLineSegment(sketch, "E60.1", {"start": v(-22.6, -47.85) * mm, "end": v(-20.2, -52) * mm});
            skLineSegment(sketch, "E60.2", {"start": v(-20.2, -52) * mm, "end": v(-22.6, -56.15) * mm});
            skLineSegment(sketch, "E60.3", {"start": v(-22.6, -56.15) * mm, "end": v(-27.4, -56.15) * mm});
            skLineSegment(sketch, "E60.4", {"start": v(-27.4, -56.15) * mm, "end": v(-29.8, -52) * mm});
            skLineSegment(sketch, "E60.5", {"start": v(-29.8, -52) * mm, "end": v(-27.4, -47.85) * mm});
            skPoint(sketch, "E60.0.midPoint", {"position": v(-25, -47.85) * mm});
            skCircle(sketch, "E61.cCircle", {"center": v(25, -52) * mm, "radius": 4.15 * mm, "construction": true});
            skLineSegment(sketch, "E61.0", {"start": v(22.6, -47.85) * mm, "end": v(27.4, -47.85) * mm});
            skLineSegment(sketch, "E61.1", {"start": v(27.4, -47.85) * mm, "end": v(29.8, -52) * mm});
            skLineSegment(sketch, "E61.2", {"start": v(29.8, -52) * mm, "end": v(27.4, -56.15) * mm});
            skLineSegment(sketch, "E61.3", {"start": v(27.4, -56.15) * mm, "end": v(22.6, -56.15) * mm});
            skLineSegment(sketch, "E61.4", {"start": v(22.6, -56.15) * mm, "end": v(20.2, -52) * mm});
            skLineSegment(sketch, "E61.5", {"start": v(20.2, -52) * mm, "end": v(22.6, -47.85) * mm});
            skPoint(sketch, "E61.0.midPoint", {"position": v(25, -47.85) * mm});
            skCircle(sketch, "E62.cCircle", {"center": v(25, -10.75) * mm, "radius": 4.15 * mm, "construction": true});
            skLineSegment(sketch, "E62.0", {"start": v(22.6, -6.6) * mm, "end": v(27.4, -6.6) * mm});
            skLineSegment(sketch, "E62.1", {"start": v(27.4, -6.6) * mm, "end": v(29.8, -10.75) * mm});
            skLineSegment(sketch, "E62.2", {"start": v(29.8, -10.75) * mm, "end": v(27.4, -14.9) * mm});
            skLineSegment(sketch, "E62.3", {"start": v(27.4, -14.9) * mm, "end": v(22.6, -14.9) * mm});
            skLineSegment(sketch, "E62.4", {"start": v(22.6, -14.9) * mm, "end": v(20.2, -10.75) * mm});
            skLineSegment(sketch, "E62.5", {"start": v(20.2, -10.75) * mm, "end": v(22.6, -6.6) * mm});
            skPoint(sketch, "E62.0.midPoint", {"position": v(25, -6.6) * mm});
            skSolve(sketch);
        }
        {
            var Q0;
            Q0=makeQuery(id+"F20.imprint","IMPRINT",FACE,{"disambiguationData":[TD([[makeQuery(id+"F20.imprint","IMPRINT",EDGE,{"derivedFrom":sQuery(id+"F20.wireOp",EDGE,"E57.0")}),-1.0]])]});
            var Q1;
            Q1=makeQuery(id+"F20.imprint","IMPRINT",FACE,{"disambiguationData":[TD([[makeQuery(id+"F20.imprint","IMPRINT",EDGE,{"derivedFrom":sQuery(id+"F20.wireOp",EDGE,"E58.0")}),-1.0]])]});
            var Q2;
            Q2=makeQuery(id+"F20.imprint","IMPRINT",FACE,{"disambiguationData":[TD([[makeQuery(id+"F20.imprint","IMPRINT",EDGE,{"derivedFrom":sQuery(id+"F20.wireOp",EDGE,"E62.0")}),-1.0]])]});
            var Q3;
            Q3=makeQuery(id+"F20.imprint","IMPRINT",FACE,{"disambiguationData":[TD([[makeQuery(id+"F20.imprint","IMPRINT",EDGE,{"derivedFrom":sQuery(id+"F20.wireOp",EDGE,"E59.0")}),-1.0]])]});
            var Q4;
            Q4=makeQuery(id+"F20.imprint","IMPRINT",FACE,{"disambiguationData":[TD([[makeQuery(id+"F20.imprint","IMPRINT",EDGE,{"derivedFrom":sQuery(id+"F20.wireOp",EDGE,"E60.0")}),-1.0]])]});
            var Q5;
            Q5=makeQuery(id+"F20.imprint","IMPRINT",FACE,{"disambiguationData":[TD([[makeQuery(id+"F20.imprint","IMPRINT",EDGE,{"derivedFrom":sQuery(id+"F20.wireOp",EDGE,"E61.0")}),-1.0]])]});
            extrude(context, id + "F21", {"entities" : qUnion([Q0, Q1, Q2, Q3, Q4, Q5]), "operationType" : NewBodyOperationType.REMOVE, "oppositeDirection" : true, "depth" : 2.5 * mm, "offsetDistance" : 25 * mm});
        }
        {
            var Q0;
            Q0=makeQuery(id+"F15.opPattern","COPY",FACE,{"derivedFrom":makeQuery(id+"F5.boolean.opBoolean","COPY",FACE,{"derivedFrom":makeQuery(id+"F5.opExtrude","CAP_FACE",FACE,{"disambiguationData":[OSD([sQuery(id+"F0.wireOp",EDGE,"E32"),sQuery(id+"F0.wireOp",EDGE,"E33")])],"isStart":false})}),"instanceName":"1"});
            var Q1;
            {var subQ0=sQuery(id+"F0.wireOp",EDGE,"E31");var subQ1=sQuery(id+"F0.wireOp",EDGE,"E15");var subQ2=sQuery(id+"F0.wireOp",EDGE,"E14");var subQ3=sQuery(id+"F0.wireOp",EDGE,"E4");var subQ4=sQuery(id+"F0.wireOp",EDGE,"E3");var subQ5=sQuery(id+"F0.wireOp",EDGE,"E2");var subQ6=sQuery(id+"F0.wireOp",EDGE,"E1");Q1=makeQuery(id+"F19.boolean.opBoolean","MERGE",FACE,{"derivedFrom":[makeQuery(id+"F16.boolean.opBoolean","MERGE",FACE,{"derivedFrom":[makeQuery(id+"F15.opPattern","COPY",FACE,{"derivedFrom":makeQuery(id+"F1.opExtrude","CAP_FACE",FACE,{"disambiguationData":[OSD([sQuery(id+"F0.wireOp",EDGE,"E0.bottom"),sQuery(id+"F0.wireOp",EDGE,"E0.top"),sQuery(id+"F0.wireOp",EDGE,"E0.left"),sQuery(id+"F0.wireOp",EDGE,"E0.right"),subQ6,subQ5,subQ4,subQ3,subQ2,subQ1,sQuery(id+"F0.wireOp",EDGE,"E25"),sQuery(id+"F0.wireOp",EDGE,"E26"),sQuery(id+"F0.wireOp",EDGE,"E27"),sQuery(id+"F0.wireOp",EDGE,"E28"),sQuery(id+"F0.wireOp",EDGE,"E29"),sQuery(id+"F0.wireOp",EDGE,"E30"),subQ0,sQuery(id+"F0.wireOp",EDGE,"E32")])],"isStart":true}),"instanceName":"1"}),makeQuery(id+"F16.opExtrude","CAP_FACE",FACE,{"disambiguationData":[OSD([subQ6,sQuery(id+"F0.wireOp",EDGE,"E23")])],"isStart":false}),makeQuery(id+"F16.opExtrude","CAP_FACE",FACE,{"disambiguationData":[OSD([subQ5,sQuery(id+"F0.wireOp",EDGE,"E24")])],"isStart":false}),makeQuery(id+"F16.opExtrude","CAP_FACE",FACE,{"disambiguationData":[OSD([subQ4,sQuery(id+"F0.wireOp",EDGE,"E19")])],"isStart":false}),makeQuery(id+"F16.opExtrude","CAP_FACE",FACE,{"disambiguationData":[OSD([subQ3,sQuery(id+"F0.wireOp",EDGE,"E20")])],"isStart":false}),makeQuery(id+"F16.opExtrude","CAP_FACE",FACE,{"disambiguationData":[OSD([subQ2,sQuery(id+"F0.wireOp",EDGE,"E21")])],"isStart":false}),makeQuery(id+"F16.opExtrude","CAP_FACE",FACE,{"disambiguationData":[OSD([subQ1,sQuery(id+"F0.wireOp",EDGE,"E22")])],"isStart":false})]}),makeQuery(id+"F19.opExtrude","CAP_FACE",FACE,{"disambiguationData":[OSD([subQ0,sQuery(id+"F17.wireOp",EDGE,"E56")])],"isStart":true})]});}
            extrude(context, id + "F22", {"entities" : qUnion([Q0]), "operationType" : NewBodyOperationType.ADD, "endBound" : BoundingType.UP_TO_SURFACE, "depth" : 25 * mm, "endBoundEntityFace" : qUnion([Q1]), "offsetDistance" : 25 * mm});
        }
        {
            var Q0;
            {var subQ0=sQuery(id+"F0.wireOp",EDGE,"E31");var subQ1=sQuery(id+"F0.wireOp",EDGE,"E15");var subQ2=sQuery(id+"F0.wireOp",EDGE,"E14");var subQ3=sQuery(id+"F0.wireOp",EDGE,"E4");var subQ4=sQuery(id+"F0.wireOp",EDGE,"E3");var subQ5=sQuery(id+"F0.wireOp",EDGE,"E2");var subQ6=sQuery(id+"F0.wireOp",EDGE,"E1");Q0=makeQuery(id+"F19.boolean.opBoolean","MERGE",FACE,{"derivedFrom":[makeQuery(id+"F16.boolean.opBoolean","MERGE",FACE,{"derivedFrom":[makeQuery(id+"F15.opPattern","COPY",FACE,{"derivedFrom":makeQuery(id+"F1.opExtrude","CAP_FACE",FACE,{"disambiguationData":[OSD([sQuery(id+"F0.wireOp",EDGE,"E0.bottom"),sQuery(id+"F0.wireOp",EDGE,"E0.top"),sQuery(id+"F0.wireOp",EDGE,"E0.left"),sQuery(id+"F0.wireOp",EDGE,"E0.right"),subQ6,subQ5,subQ4,subQ3,sQuery(id+"F0.wireOp",EDGE,"E8.bottom"),sQuery(id+"F0.wireOp",EDGE,"E8.top"),sQuery(id+"F0.wireOp",EDGE,"E8.left"),sQuery(id+"F0.wireOp",EDGE,"E8.right"),sQuery(id+"F0.wireOp",EDGE,"E9.filletArc"),sQuery(id+"F0.wireOp",EDGE,"E10.filletArc"),sQuery(id+"F0.wireOp",EDGE,"E11.filletArc"),sQuery(id+"F0.wireOp",EDGE,"E12.filletArc"),subQ2,subQ1,sQuery(id+"F0.wireOp",EDGE,"E25"),sQuery(id+"F0.wireOp",EDGE,"E26"),sQuery(id+"F0.wireOp",EDGE,"E27"),sQuery(id+"F0.wireOp",EDGE,"E28"),sQuery(id+"F0.wireOp",EDGE,"E29"),sQuery(id+"F0.wireOp",EDGE,"E30"),subQ0])],"isStart":true}),"instanceName":"1"}),makeQuery(id+"F16.opExtrude","CAP_FACE",FACE,{"disambiguationData":[OSD([subQ6,sQuery(id+"F0.wireOp",EDGE,"E23")])],"isStart":false}),makeQuery(id+"F16.opExtrude","CAP_FACE",FACE,{"disambiguationData":[OSD([subQ5,sQuery(id+"F0.wireOp",EDGE,"E24")])],"isStart":false}),makeQuery(id+"F16.opExtrude","CAP_FACE",FACE,{"disambiguationData":[OSD([subQ4,sQuery(id+"F0.wireOp",EDGE,"E19")])],"isStart":false}),makeQuery(id+"F16.opExtrude","CAP_FACE",FACE,{"disambiguationData":[OSD([subQ3,sQuery(id+"F0.wireOp",EDGE,"E20")])],"isStart":false}),makeQuery(id+"F16.opExtrude","CAP_FACE",FACE,{"disambiguationData":[OSD([subQ2,sQuery(id+"F0.wireOp",EDGE,"E21")])],"isStart":false}),makeQuery(id+"F16.opExtrude","CAP_FACE",FACE,{"disambiguationData":[OSD([subQ1,sQuery(id+"F0.wireOp",EDGE,"E22")])],"isStart":false}),makeQuery(id+"F16.opExtrude","CAP_FACE",FACE,{"disambiguationData":[OSD([sQuery(id+"FN2gQwAAYemFBsZ_1.wireOp",EDGE,"b6049740-b090-4d88-954d-f700c698196f.0"),sQuery(id+"FN2gQwAAYemFBsZ_1.wireOp",EDGE,"f422f45c-7bf5-412d-89e3-80266b48b357.0"),sQuery(id+"FN2gQwAAYemFBsZ_1.wireOp",EDGE,"efcb35ef-2e5b-4bb8-b79f-5e92435b3e5b.0"),sQuery(id+"FN2gQwAAYemFBsZ_1.wireOp",EDGE,"1646675d-dff0-4150-a587-2e2e2abf0155.0"),sQuery(id+"FN2gQwAAYemFBsZ_1.wireOp",EDGE,"c82016d3-8c5d-4273-b2c0-3a98afdc202d.0"),sQuery(id+"FN2gQwAAYemFBsZ_1.wireOp",EDGE,"76cfad24-abf5-450d-8950-0da708049a1b.0"),sQuery(id+"FN2gQwAAYemFBsZ_1.wireOp",EDGE,"2f079088-94a9-4a35-b1d6-c113e9922d5e.0"),sQuery(id+"FN2gQwAAYemFBsZ_1.wireOp",EDGE,"c33eaa7b-eaf1-4da6-90ec-c160ff7c63d3.0"),sQuery(id+"FN2gQwAAYemFBsZ_1.wireOp",EDGE,"f0ed33f3-9ef4-43dd-9b29-648670789cae.0"),sQuery(id+"FN2gQwAAYemFBsZ_1.wireOp",EDGE,"f0ed33f3-9ef4-43dd-9b29-648670789cae.1"),sQuery(id+"FN2gQwAAYemFBsZ_1.wireOp",EDGE,"f0ed33f3-9ef4-43dd-9b29-648670789cae.2"),sQuery(id+"FN2gQwAAYemFBsZ_1.wireOp",EDGE,"f0ed33f3-9ef4-43dd-9b29-648670789cae.3"),sQuery(id+"FN2gQwAAYemFBsZ_1.wireOp",EDGE,"f0ed33f3-9ef4-43dd-9b29-648670789cae.4"),sQuery(id+"FN2gQwAAYemFBsZ_1.wireOp",EDGE,"f0ed33f3-9ef4-43dd-9b29-648670789cae.5"),sQuery(id+"FN2gQwAAYemFBsZ_1.wireOp",EDGE,"f0ed33f3-9ef4-43dd-9b29-648670789cae.6"),sQuery(id+"FN2gQwAAYemFBsZ_1.wireOp",EDGE,"f0ed33f3-9ef4-43dd-9b29-648670789cae.7")])],"isStart":false})]}),makeQuery(id+"F19.opExtrude","CAP_FACE",FACE,{"disambiguationData":[OSD([subQ0,sQuery(id+"F17.wireOp",EDGE,"E56")])],"isStart":true})]});}
            var sketch = newSketch(context, id + "F23", { "sketchPlane" : qUnion([Q0])});
            skCircle(sketch, "E63.cCircle", {"center": v(0, -16.9) * mm, "radius": 4.05 * mm, "construction": true});
            skLineSegment(sketch, "E63.0", {"start": v(-2.34, -12.85) * mm, "end": v(2.34, -12.85) * mm});
            skLineSegment(sketch, "E63.1", {"start": v(2.34, -12.85) * mm, "end": v(4.68, -16.9) * mm});
            skLineSegment(sketch, "E63.2", {"start": v(4.68, -16.9) * mm, "end": v(2.34, -20.95) * mm});
            skLineSegment(sketch, "E63.3", {"start": v(2.34, -20.95) * mm, "end": v(-2.34, -20.95) * mm});
            skLineSegment(sketch, "E63.4", {"start": v(-2.34, -20.95) * mm, "end": v(-4.68, -16.9) * mm});
            skLineSegment(sketch, "E63.5", {"start": v(-4.68, -16.9) * mm, "end": v(-2.34, -12.85) * mm});
            skPoint(sketch, "E63.0.midPoint", {"position": v(0, -12.85) * mm});
            skSolve(sketch);
        }
        {
            var Q0;
            {var subQ0=sQuery(id+"F23.wireOp",EDGE,"8Jgyktpu-3GaS-8qby-PXar-nOVilq71KfF4");Q0=makeQuery(id+"F23.imprint","IMPRINT",FACE,{"disambiguationData":[TD([[makeQuery(id+"F23.imprint","IMPRINT",EDGE,{"derivedFrom":subQ0}),-1.0]])]});}
            var Q1;
            Q1=makeQuery(id+"F23.imprint","IMPRINT",FACE,{"disambiguationData":[TD([[makeQuery(id+"F23.imprint","IMPRINT",EDGE,{"derivedFrom":sQuery(id+"F23.wireOp",EDGE,"E63.0")}),-1.0]])]});
            var Q2;
            Q2=makeQuery(id+"F23.imprint","IMPRINT",FACE,{"disambiguationData":[TD([[makeQuery(id+"F23.imprint","IMPRINT",EDGE,{"derivedFrom":sQuery(id+"F23.wireOp",EDGE,"83f5faf3-ebc1-4569-a82a-d42b1f0784ee.0")}),-1.0]])]});
            var Q3;
            {var subQ0=sQuery(id+"F23.wireOp",EDGE,"xsZvV7ms-YUi7-CpOk-WE9B-vCxr27DNhaBx");Q3=makeQuery(id+"F23.imprint","IMPRINT",FACE,{"disambiguationData":[TD([[makeQuery(id+"F23.imprint","IMPRINT",EDGE,{"derivedFrom":subQ0}),1.0]])]});}
            var Q4;
            {var subQ0=sQuery(id+"F23.wireOp",EDGE,"83f5faf3-ebc1-4569-a82a-d42b1f0784ee.2");var subQ1=sQuery(id+"F23.wireOp",EDGE,"E63.4");var subQ2=makeQuery(id+"F23.imprint","INTERSECT",VERTEX,{"derivedFrom":[subQ1,subQ0]});Q4=makeQuery(id+"F23.imprint","IMPRINT",FACE,{"disambiguationData":[TD([[makeQuery(id+"F23.imprint","IMPRINT",EDGE,{"disambiguationData":[TD([[subQ2,1.0]])],"derivedFrom":subQ1}),-1.0]])]});}
            var Q5;
            {var subQ0=sQuery(id+"F23.wireOp",EDGE,"83f5faf3-ebc1-4569-a82a-d42b1f0784ee.4");var subQ1=sQuery(id+"F23.wireOp",EDGE,"E63.2");var subQ2=makeQuery(id+"F23.imprint","INTERSECT",VERTEX,{"derivedFrom":[subQ1,subQ0]});Q5=makeQuery(id+"F23.imprint","IMPRINT",FACE,{"disambiguationData":[TD([[makeQuery(id+"F23.imprint","IMPRINT",EDGE,{"disambiguationData":[TD([[subQ2,-1.0]])],"derivedFrom":subQ1}),-1.0]])]});}
            extrude(context, id + "F24", {"entities" : qUnion([Q0, Q1, Q2, Q3, Q4, Q5]), "operationType" : NewBodyOperationType.REMOVE, "oppositeDirection" : true, "depth" : 2.5 * mm, "offsetDistance" : 25 * mm});
        }
        {
            var Q0;
            Q0=makeQuery(id+"F15.opPattern","COPY",EDGE,{"derivedFrom":makeQuery(id+"F1.opExtrude","SWEPT_EDGE",EDGE,{"disambiguationData":[OSD([sQuery(id+"F0.wireOp",EDGE,"E0.bottom"),sQuery(id+"F0.wireOp",EDGE,"E0.left")])]}),"instanceName":"1"});
            var Q1;
            Q1=makeQuery(id+"F15.opPattern","COPY",EDGE,{"derivedFrom":makeQuery(id+"F1.opExtrude","SWEPT_EDGE",EDGE,{"disambiguationData":[OSD([sQuery(id+"F0.wireOp",EDGE,"E0.bottom"),sQuery(id+"F0.wireOp",EDGE,"E0.right")])]}),"instanceName":"1"});
            var Q2;
            Q2=makeQuery(id+"F1.opExtrude","SWEPT_EDGE",EDGE,{"disambiguationData":[OSD([sQuery(id+"F0.wireOp",EDGE,"E0.bottom"),sQuery(id+"F0.wireOp",EDGE,"E0.right")])]});
            var Q3;
            Q3=makeQuery(id+"F1.opExtrude","SWEPT_EDGE",EDGE,{"disambiguationData":[OSD([sQuery(id+"F0.wireOp",EDGE,"E0.bottom"),sQuery(id+"F0.wireOp",EDGE,"E0.left")])]});
            var Q4;
            Q4=makeQuery(id+"F1.opExtrude","SWEPT_EDGE",EDGE,{"disambiguationData":[OSD([sQuery(id+"F0.wireOp",EDGE,"E0.top"),sQuery(id+"F0.wireOp",EDGE,"E0.left")])]});
            var Q5;
            Q5=makeQuery(id+"F1.opExtrude","SWEPT_EDGE",EDGE,{"disambiguationData":[OSD([sQuery(id+"F0.wireOp",EDGE,"E0.top"),sQuery(id+"F0.wireOp",EDGE,"E0.right")])]});
            var Q6;
            Q6=makeQuery(id+"F15.opPattern","COPY",EDGE,{"derivedFrom":makeQuery(id+"F1.opExtrude","SWEPT_EDGE",EDGE,{"disambiguationData":[OSD([sQuery(id+"F0.wireOp",EDGE,"E0.top"),sQuery(id+"F0.wireOp",EDGE,"E0.right")])]}),"instanceName":"1"});
            var Q7;
            Q7=makeQuery(id+"F15.opPattern","COPY",EDGE,{"derivedFrom":makeQuery(id+"F1.opExtrude","SWEPT_EDGE",EDGE,{"disambiguationData":[OSD([sQuery(id+"F0.wireOp",EDGE,"E0.top"),sQuery(id+"F0.wireOp",EDGE,"E0.left")])]}),"instanceName":"1"});
            fillet(context, id + "F25", {"entities" : qUnion([Q0, Q1, Q2, Q3, Q4, Q5, Q6, Q7]), "radius" : 8 * mm, "tangentPropagation" : true, "allowEdgeOverflow" : false});
        }
    });
